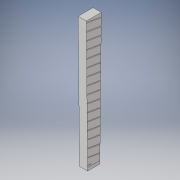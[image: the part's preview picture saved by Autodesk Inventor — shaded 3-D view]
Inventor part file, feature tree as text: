
AUTODESK INVENTOR PART (.ipt)
format: ipt  version: 2018 (Build 220112000, 112)  size: 1,891,840 bytes
history: native  units: in
note: dims shown in document units (in); Inventor stores cm internally (conversion verified against a paired STEP export)
features: sketch x13, extrude x12, other x7, plane x5, mirror x3, reference x3, projected_geometry x3, surface_op x1, loft x1, direct_edit x1
ambient origin geometry x8: Origin, YZ Plane, XZ Plane, XY Plane, X Axis, Y Axis, Z Axis, Center Point
bodies: Solid1 (feature_tree)
feature tree (49):
  extrude  "Extrusion1"  Depth=3.0in
  extrude  "Extrusion2"  Depth=1.0in TaperAngle=0.0deg
  extrude  "Extrusion3"  Depth=3.0in TaperAngle=0.0deg
  extrude  "Extrusion4"  Depth=3.0in TaperAngle=0.0deg
  extrude  "Extrusion5"  Depth=7.25in TaperAngle=0.0deg
  plane  "Work Plane1"
  plane  "Work Plane2"
  mirror  "Mirror1"
  mirror  "Mirror2"
  extrude  "Extrusion6"  Depth=0.25in
  surface_op  "Sculpt1"
  extrude  "Extrusion7"  Depth=2.0in TaperAngle=0.0deg
  extrude  "Extrusion9"  Depth=11.811in TaperAngle=0.0deg
  extrude  "Extrusion10"  TaperAngle=0.0deg  [1 undecoded]
  extrude  "Extrusion13"  Depth=0.3937in
  loft  "Loft1"
  direct_edit  "Direct Edit2"
  extrude  "Extrusion16"  [1 undecoded]
  plane  "Work Plane3"
  extrude  "Extrusion18"  [1 undecoded]
  plane  "Work Plane5"
  mirror  "Mirror3"
  sketch  "Sketch1"  dims[d0=1.0in d1=3.0in]
  sketch  "Sketch3"  dims[d2=1.0in d3=0.0in d4=1.0in d5=0.0in]
  sketch  "Sketch4"  dims[d6=1.0in d7=0.0in d8=3.0in d9=0.0in]
  reference  "Reference1"
  sketch  "Sketch5"  dims[d10=0.3in d11=3.0in d12=0.0in]
  reference  "Reference2"
  reference  "Reference3"
  sketch  "Sketch6"  dims[d13=7.25in d14=0.0in d15=7.25in d16=0.0in]
  sketch  "Sketch7"  dims[d19=0.25in d20=0.25in]
  projected_geometry  "Projected Loop1"
  sketch  "Sketch8"  dims[d21=2.0in d22=0.0in d23=2.0in d24=0.0in]
  sketch  "Sketch10"  dims[d36=0.0148in d37=11.811in d38=0.0in]
  sketch  "Sketch11"  dims[d39=0.0074in d40=0.0in d41=90.0deg]
  sketch  "Sketch14"  dims[d42=0.0in d43=90.0deg d44=0.3937in d45=0.374in d46=0.374in]
  sketch  "Sketch15"  dims[d52=0.1969in d53=0.0in d63=11.811in d64=0.0in]
  projected_geometry  "Projected Loop2"
  other  "Edges1"
  sketch  "Sketch18"  dims[d65=90.0deg d66=-0.3937in]
  projected_geometry  "Projected Loop3"
  sketch  "Sketch22"
  plane  "Work Plane4"
  other  "<userpath>\Desktop\spring jig.iam"
  other  "spring jig.iam"
  other  "AR-15 GI Magazine Spring Uncompressed:1"
  other  "Composite1"
  other  "Srf1"
  other  "Scale2"
note: 3 required parameter values undecoded (feature->parameter linkage not recoverable at this tier; creation-order binding heuristic only, values carry confidence <= 0.55)
